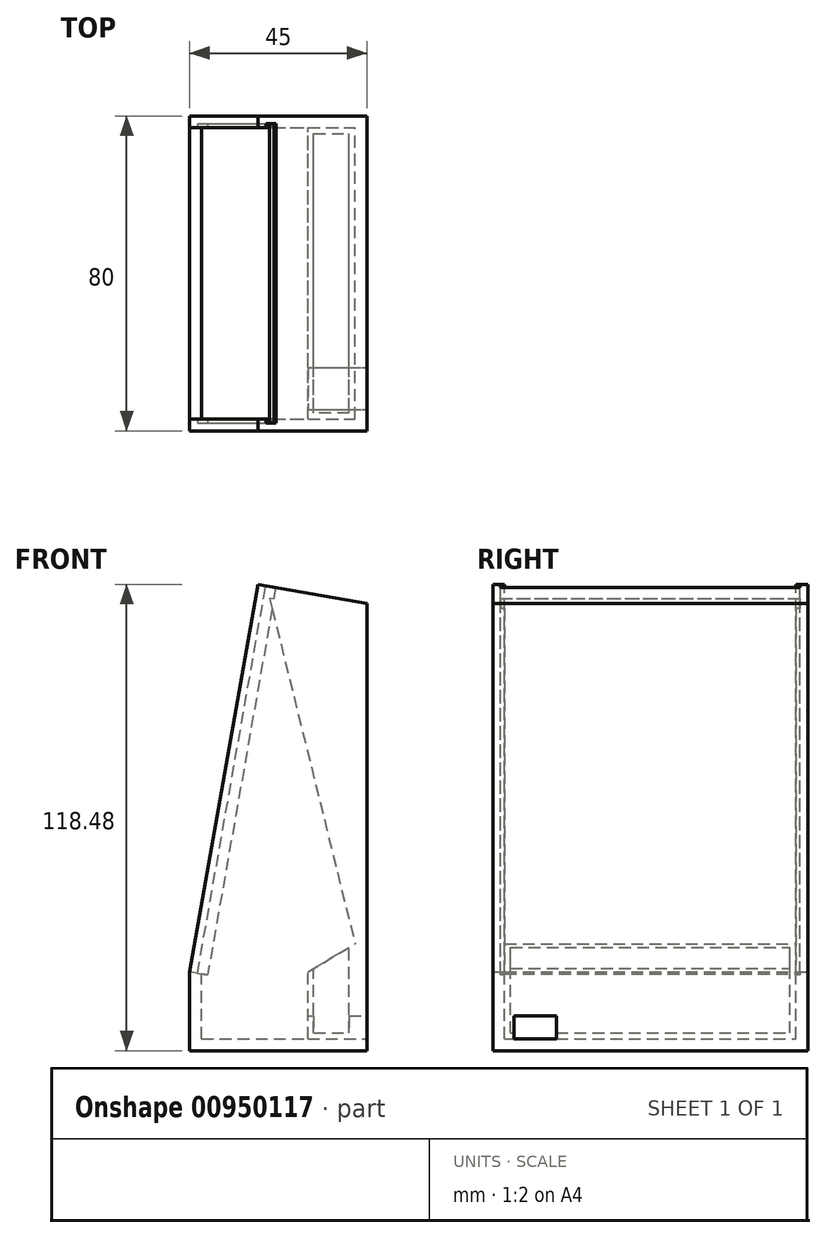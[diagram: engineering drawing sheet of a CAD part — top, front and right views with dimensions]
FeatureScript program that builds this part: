
annotation { "Feature Type Name" : "Feature", "Feature Type Description" : "" }
export const myFeature = defineFeature(function(context is Context, id is Id, definition is map)
    precondition{}
    {
        {
            var Q0;
            Q0=qCreatedBy(makeId("Front.planeOp"),FACE);
            var sketch = newSketch(context, id + "F0", { "sketchPlane" : qUnion([Q0])});
            skLineSegment(sketch, "E0.bottom", {"start": v(0, 0) * mm, "end": v(45, 0) * mm});
            skLineSegment(sketch, "E0.top", {"start": v(0, 20) * mm, "end": v(45, 20) * mm, "construction": true});
            skLineSegment(sketch, "E0.left", {"start": v(0, 0) * mm, "end": v(0, 20) * mm});
            skLineSegment(sketch, "E0.right", {"start": v(45, 0) * mm, "end": v(45, 20) * mm});
            skLineSegment(sketch, "E1", {"start": v(0, 20) * mm, "end": v(17.36, 118.48) * mm});
            skLineSegment(sketch, "E2", {"start": v(17.36, 118.48) * mm, "end": v(45, 113.6) * mm});
            skLineSegment(sketch, "E3", {"start": v(45, 113.6) * mm, "end": v(45, 20) * mm});
            skLineSegment(sketch, "E4", {"start": v(45, 3) * mm, "end": v(42, 3) * mm, "construction": true});
            skLineSegment(sketch, "E5", {"start": v(3, 0) * mm, "end": v(3, 37.01) * mm, "construction": true});
            skLineSegment(sketch, "E6", {"start": v(42, 0) * mm, "end": v(42, 114.14) * mm});
            skLineSegment(sketch, "E7.bottom", {"start": v(3, 3) * mm, "end": v(30, 3) * mm, "construction": true});
            skLineSegment(sketch, "E7.top", {"start": v(3, 20) * mm, "end": v(30, 20) * mm, "construction": true});
            skLineSegment(sketch, "E7.left", {"start": v(3, 3) * mm, "end": v(3, 20) * mm, "construction": true});
            skLineSegment(sketch, "E7.right", {"start": v(30, 3) * mm, "end": v(30, 20) * mm});
            skLineSegment(sketch, "E8", {"start": v(30, 20) * mm, "end": v(42, 27.18) * mm});
            skLineSegment(sketch, "E9", {"start": v(42, 27.18) * mm, "end": v(42, 3) * mm});
            skLineSegment(sketch, "E10", {"start": v(30, 3) * mm, "end": v(0, 3) * mm, "construction": true});
            skLineSegment(sketch, "E11", {"start": v(42, 3) * mm, "end": v(30, 3) * mm});
            skLineSegment(sketch, "E12", {"start": v(36, 23.6) * mm, "end": v(8.68, 69.24) * mm, "construction": true});
            skLineSegment(sketch, "E13", {"start": v(42, 27.18) * mm, "end": v(20.3, 114.92) * mm});
            skLineSegment(sketch, "E14", {"start": v(20.3, 114.92) * mm, "end": v(42, 111.1) * mm});
            skSolve(sketch);
        }
        {
            var Q0;
            {var subQ0=sQuery(id+"F0.wireOp",EDGE,"E1");Q0=makeQuery(id+"F0.imprint","IMPRINT",FACE,{"disambiguationData":[TD([[makeQuery(id+"F0.imprint","IMPRINT",EDGE,{"derivedFrom":subQ0}),-1.0]])]});}
            var Q1;
            {var subQ0=sQuery(id+"F0.wireOp",EDGE,"E0.left");Q1=makeQuery(id+"F0.imprint","IMPRINT",FACE,{"disambiguationData":[TD([[makeQuery(id+"F0.imprint","IMPRINT",EDGE,{"derivedFrom":subQ0}),-1.0]])]});}
            var Q2;
            {var subQ0=sQuery(id+"F0.wireOp",EDGE,"E0.right");Q2=makeQuery(id+"F0.imprint","IMPRINT",FACE,{"disambiguationData":[TD([[makeQuery(id+"F0.imprint","IMPRINT",EDGE,{"derivedFrom":subQ0}),1.0]])]});}
            var Q3;
            Q3=makeQuery(id+"F0.imprint","IMPRINT",FACE,{"disambiguationData":[TD([[makeQuery(id+"F0.imprint","IMPRINT",EDGE,{"derivedFrom":sQuery(id+"F0.wireOp",EDGE,"E7.right")}),-1.0]])]});
            var Q4;
            {var subQ0=sQuery(id+"F0.wireOp",EDGE,"E13");Q4=makeQuery(id+"F0.imprint","IMPRINT",FACE,{"disambiguationData":[TD([[makeQuery(id+"F0.imprint","IMPRINT",EDGE,{"derivedFrom":subQ0}),-1.0]])]});}
            extrude(context, id + "F1", {"entities" : qUnion([Q0, Q1, Q2, Q3, Q4]), "endBound" : BoundingType.SYMMETRIC, "depth" : 80 * mm, "offsetDistance" : 25 * mm});
        }
        {
            var Q0;
            Q0=makeQuery(id+"F4.boolean.opBoolean","COPY",FACE,{"derivedFrom":makeQuery(id+"F4.opExtrude","SWEPT_FACE",FACE,{"disambiguationData":[OSD([sQuery(id+"F3.wireOp",EDGE,"E15.right")])]})});
            var Q1;
            Q1=makeQuery(id+"F1.opExtrude","SWEPT_FACE",FACE,{"disambiguationData":[OSD([sQuery(id+"F0.wireOp",EDGE,"E1")])]});
            var Q2;
            Q2=makeQuery(id+"F1.opExtrude","SWEPT_BODY",BODY,{"disambiguationData":[OSD([sQuery(id+"F0.wireOp",EDGE,"E0.bottom"),sQuery(id+"F0.wireOp",EDGE,"E0.left"),sQuery(id+"F0.wireOp",EDGE,"E0.right"),sQuery(id+"F0.wireOp",EDGE,"E1"),sQuery(id+"F0.wireOp",EDGE,"E2"),sQuery(id+"F0.wireOp",EDGE,"E3")])]});
            shell(context, id + "F2", {"isHollow" : true, "entities" : qUnion([Q0, Q1]), "parts" : qUnion([Q2]), "thickness" : 3 * mm});
        }
        {
            var Q0;
            Q0=makeQuery(id+"F1.opExtrude","SWEPT_FACE",FACE,{"disambiguationData":[OSD([sQuery(id+"F0.wireOp",EDGE,"E2")])]});
            var sketch = newSketch(context, id + "F3", { "sketchPlane" : qUnion([Q0])});
            skLineSegment(sketch, "E15.bottom", {"start": v(-1.47, 38) * mm, "end": v(1.13, 38) * mm});
            skLineSegment(sketch, "E15.top", {"start": v(-1.47, -38) * mm, "end": v(1.13, -38) * mm});
            skLineSegment(sketch, "E15.left", {"start": v(-1.47, 38) * mm, "end": v(-1.47, -38) * mm});
            skLineSegment(sketch, "E15.right", {"start": v(1.13, 38) * mm, "end": v(1.13, -38) * mm});
            skLineSegment(sketch, "E16", {"start": v(-1.47, 37) * mm, "end": v(-3.47, 37) * mm});
            skLineSegment(sketch, "E17", {"start": v(-1.47, -37) * mm, "end": v(-3.47, -37) * mm});
            skSolve(sketch);
        }
        {
            var Q0;
            {var subQ3=sQuery(id+"F3.wireOp",EDGE,"E15.bottom");Q0=makeQuery(id+"F3.imprint","IMPRINT",FACE,{"disambiguationData":[TD([[makeQuery(id+"F3.imprint","IMPRINT",EDGE,{"derivedFrom":subQ3}),-1.0]])]});}
            var Q1;
            {var subQ0=sQuery(id+"F3.wireOp",EDGE,"E16");Q1=makeQuery(id+"F3.imprint","IMPRINT",FACE,{"disambiguationData":[TD([[makeQuery(id+"F3.imprint","IMPRINT",EDGE,{"derivedFrom":subQ0}),1.0]])]});}
            extrude(context, id + "F4", {"entities" : qUnion([Q0, Q1]), "operationType" : NewBodyOperationType.REMOVE, "oppositeDirection" : true, "depth" : 100 * mm, "offsetDistance" : 25 * mm});
        }
        {
            var Q0;
            Q0=makeQuery(id+"F0.imprint","IMPRINT",FACE,{"disambiguationData":[TD([[makeQuery(id+"F0.imprint","IMPRINT",EDGE,{"derivedFrom":sQuery(id+"F0.wireOp",EDGE,"E7.right")}),-1.0]])]});
            var Q1;
            {var subQ0=sQuery(id+"F0.wireOp",EDGE,"E3");var subQ1=sQuery(id+"F0.wireOp",EDGE,"E2");var subQ2=sQuery(id+"F0.wireOp",EDGE,"E1");var subQ3=sQuery(id+"F0.wireOp",EDGE,"E0.right");var subQ4=sQuery(id+"F0.wireOp",EDGE,"E0.left");var subQ5=sQuery(id+"F0.wireOp",EDGE,"E0.bottom");Q1=makeQuery(id+"F2.opShell","OFFSET_FACE",FACE,{"disambiguationData":[OSD([subQ5,subQ4,subQ3,subQ2,subQ1,subQ0]),TDD([makeQuery(id+"F1.opExtrude","CAP_FACE",FACE,{"disambiguationData":[OSD([subQ5,subQ4,subQ3,subQ2,subQ1,subQ0])],"isStart":false})])]});}
            var Q2;
            {var subQ0=sQuery(id+"F0.wireOp",EDGE,"E3");var subQ1=sQuery(id+"F0.wireOp",EDGE,"E2");var subQ2=sQuery(id+"F0.wireOp",EDGE,"E1");var subQ3=sQuery(id+"F0.wireOp",EDGE,"E0.right");var subQ4=sQuery(id+"F0.wireOp",EDGE,"E0.left");var subQ5=sQuery(id+"F0.wireOp",EDGE,"E0.bottom");Q2=makeQuery(id+"F2.opShell","OFFSET_FACE",FACE,{"disambiguationData":[OSD([subQ5,subQ4,subQ3,subQ2,subQ1,subQ0]),TDD([makeQuery(id+"F1.opExtrude","CAP_FACE",FACE,{"disambiguationData":[OSD([subQ5,subQ4,subQ3,subQ2,subQ1,subQ0])],"isStart":true})])]});}
            extrude(context, id + "F5", {"entities" : qUnion([Q0]), "endBound" : BoundingType.UP_TO_SURFACE, "depth" : 74 * mm, "endBoundEntityFace" : qUnion([Q1]), "offsetDistance" : 25 * mm, "hasSecondDirection" : true, "secondDirectionBound" : SecondDirectionBoundingType.UP_TO_SURFACE, "secondDirectionOppositeDirection" : true, "secondDirectionDepth" : 25 * mm, "secondDirectionBoundEntityFace" : qUnion([Q2])});
        }
        {
            var Q0;
            Q0=makeQuery(id+"F5.opExtrude","SWEPT_FACE",FACE,{"disambiguationData":[OSD([sQuery(id+"F0.wireOp",EDGE,"E8")])]});
            var Q1;
            Q1=makeQuery(id+"F5.opExtrude","SWEPT_BODY",BODY,{"disambiguationData":[OSD([sQuery(id+"F0.wireOp",EDGE,"E7.right"),sQuery(id+"F0.wireOp",EDGE,"E8"),sQuery(id+"F0.wireOp",EDGE,"E9"),sQuery(id+"F0.wireOp",EDGE,"E11")])]});
            shell(context, id + "F6", {"entities" : qUnion([Q0]), "parts" : qUnion([Q1]), "thickness" : 1.5 * mm});
        }
        {
            var Q0;
            {var subQ0=sQuery(id+"F0.wireOp",EDGE,"E13");Q0=makeQuery(id+"F0.imprint","IMPRINT",FACE,{"disambiguationData":[TD([[makeQuery(id+"F0.imprint","IMPRINT",EDGE,{"derivedFrom":subQ0}),-1.0]])]});}
            extrude(context, id + "F7", {"entities" : qUnion([Q0]), "operationType" : NewBodyOperationType.ADD, "endBound" : BoundingType.SYMMETRIC, "depth" : 80 * mm, "offsetDistance" : 25 * mm});
        }
        {
            var Q0;
            Q0=makeQuery(id+"F1.opExtrude","SWEPT_FACE",FACE,{"disambiguationData":[OSD([sQuery(id+"F0.wireOp",EDGE,"E0.right"),sQuery(id+"F0.wireOp",EDGE,"E3")])]});
            var sketch = newSketch(context, id + "F8", { "sketchPlane" : qUnion([Q0])});
            skLineSegment(sketch, "E18.bottom", {"start": v(-23.87, 3) * mm, "end": v(-34.62, 3) * mm});
            skLineSegment(sketch, "E18.top", {"start": v(-23.87, 8.8) * mm, "end": v(-34.62, 8.8) * mm});
            skLineSegment(sketch, "E18.left", {"start": v(-23.87, 3) * mm, "end": v(-23.87, 8.8) * mm});
            skLineSegment(sketch, "E18.right", {"start": v(-34.62, 3) * mm, "end": v(-34.62, 8.8) * mm});
            skCircle(sketch, "E19", {"center": v(-36.7, 5.9) * mm, "radius": 1.02 * mm, "construction": true});
            skCircle(sketch, "E20", {"center": v(-21.8, 5.9) * mm, "radius": 1.02 * mm, "construction": true});
            skPoint(sketch, "E20.centerSnap0", {"position": v(-23.87, 5.9) * mm});
            skPoint(sketch, "E21", {"position": v(-34.62, 5.9) * mm});
            skLineSegment(sketch, "E22.bottom", {"start": v(-19.5, 8.15) * mm, "end": v(-39, 8.15) * mm, "construction": true});
            skLineSegment(sketch, "E22.top", {"start": v(-19.5, 3.65) * mm, "end": v(-39, 3.65) * mm, "construction": true});
            skLineSegment(sketch, "E22.left", {"start": v(-19.5, 8.15) * mm, "end": v(-19.5, 3.65) * mm, "construction": true});
            skLineSegment(sketch, "E22.right", {"start": v(-39, 8.15) * mm, "end": v(-39, 3.65) * mm, "construction": true});
            skPoint(sketch, "E22.middle", {"position": v(-29.25, 5.9) * mm});
            skPoint(sketch, "E22.middle.positionSnap0", {"position": v(-29.25, 8.8) * mm});
            skPoint(sketch, "E22.centerSnap0", {"position": v(-29.25, 8.8) * mm});
            skCircle(sketch, "E23.0", {"center": v(-36.7, 5.9) * mm, "radius": 0.82 * mm, "construction": true});
            skCircle(sketch, "E24.0", {"center": v(-21.8, 5.9) * mm, "radius": 0.77 * mm, "construction": true});
            skSolve(sketch);
        }
        {
            var Q0;
            Q0=makeQuery(id+"F8.imprint","IMPRINT",FACE,{"disambiguationData":[TD([[makeQuery(id+"F8.imprint","IMPRINT",EDGE,{"derivedFrom":sQuery(id+"F8.wireOp",EDGE,"E18.bottom")}),-1.0]])]});
            var Q1;
            Q1=makeQuery(id+"F5.opExtrude","SWEPT_FACE",FACE,{"disambiguationData":[OSD([sQuery(id+"F0.wireOp",EDGE,"E7.right")])]});
            extrude(context, id + "F9", {"entities" : qUnion([Q0]), "operationType" : NewBodyOperationType.REMOVE, "endBound" : BoundingType.UP_TO_SURFACE, "oppositeDirection" : true, "depth" : 19.5 * mm, "endBoundEntityFace" : qUnion([Q1]), "offsetDistance" : 25 * mm});
        }
    });
